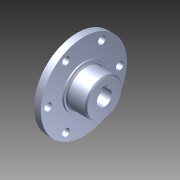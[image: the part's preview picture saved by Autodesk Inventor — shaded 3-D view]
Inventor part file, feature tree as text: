
AUTODESK INVENTOR PART (.ipt)
format: ipt  version: 2015 (Build 190159000, 159)  size: 158,720 bytes
history: native  units: in
note: dims shown in document units (in); Inventor stores cm internally (conversion verified against a paired STEP export)
features: chamfer x1, other x1, imported_body x1
ambient origin geometry x8: Origin, YZ Plane, XZ Plane, XY Plane, X Axis, Y Axis, Z Axis, Center Point
bodies: Body1 (feature_tree)
feature tree (3):
  chamfer  "Chamfer2"  [1 undecoded]
  other  "am-0985a 10mm key hub1"
  imported_body  "Base1"
note: 1 required parameter value undecoded (feature->parameter linkage not recoverable at this tier; creation-order binding heuristic only, values carry confidence <= 0.55)
